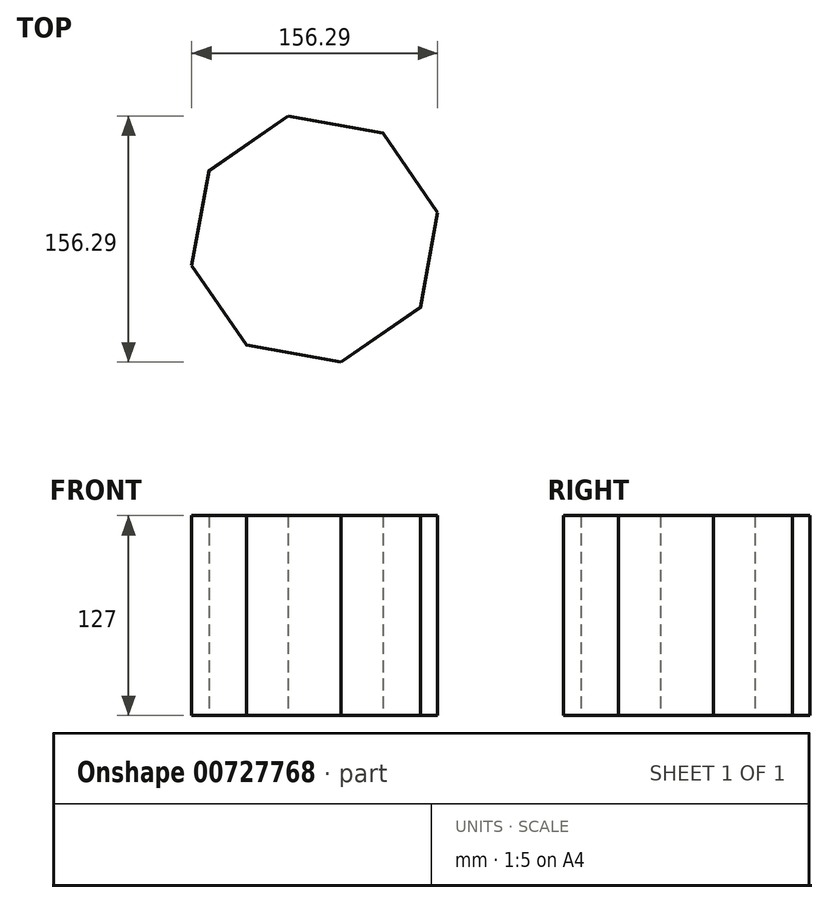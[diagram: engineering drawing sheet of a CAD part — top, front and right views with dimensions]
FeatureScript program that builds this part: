
annotation { "Feature Type Name" : "Feature", "Feature Type Description" : "" }
export const myFeature = defineFeature(function(context is Context, id is Id, definition is map)
    precondition{}
    {
        {
            var Q0;
            Q0=qCreatedBy(makeId("Top.planeOp"),FACE);
            var sketch = newSketch(context, id + "F0", { "sketchPlane" : qUnion([Q0])});
            skCircle(sketch, "E0.cCircle", {"center": v(-104, 22.78) * mm, "radius": 73.86 * mm, "construction": true});
            skLineSegment(sketch, "E0.0", {"start": v(-60.66, 89.95) * mm, "end": v(-25.86, 39.63) * mm});
            skLineSegment(sketch, "E0.1", {"start": v(-25.86, 39.63) * mm, "end": v(-36.84, -20.56) * mm});
            skLineSegment(sketch, "E0.2", {"start": v(-36.84, -20.56) * mm, "end": v(-87.16, -55.36) * mm});
            skLineSegment(sketch, "E0.3", {"start": v(-87.16, -55.36) * mm, "end": v(-147.35, -44.39) * mm});
            skLineSegment(sketch, "E0.4", {"start": v(-147.35, -44.39) * mm, "end": v(-182.15, 5.93) * mm});
            skLineSegment(sketch, "E0.5", {"start": v(-182.15, 5.93) * mm, "end": v(-171.18, 66.13) * mm});
            skLineSegment(sketch, "E0.6", {"start": v(-171.18, 66.13) * mm, "end": v(-120.86, 100.93) * mm});
            skLineSegment(sketch, "E0.7", {"start": v(-120.86, 100.93) * mm, "end": v(-60.66, 89.95) * mm});
            skPoint(sketch, "E0.0.midPoint", {"position": v(-43.26, 64.8) * mm});
            skSolve(sketch);
        }
        {
            var Q0;
            Q0=makeQuery(id+"F0.imprint","IMPRINT",FACE,{"disambiguationData":[TD([[makeQuery(id+"F0.imprint","IMPRINT",EDGE,{"derivedFrom":sQuery(id+"F0.wireOp",EDGE,"E0.0")}),-1.0]])]});
            extrude(context, id + "F1", {"entities" : qUnion([Q0]), "depth" : 127 * mm, "offsetDistance" : 25.4 * mm});
        }
        {
            var Q0;
            Q0=makeQuery(id+"F1.opExtrude","CAP_FACE",FACE,{"disambiguationData":[OSD([sQuery(id+"F0.wireOp",EDGE,"E0.0"),sQuery(id+"F0.wireOp",EDGE,"E0.1"),sQuery(id+"F0.wireOp",EDGE,"E0.2"),sQuery(id+"F0.wireOp",EDGE,"E0.3"),sQuery(id+"F0.wireOp",EDGE,"E0.4"),sQuery(id+"F0.wireOp",EDGE,"E0.5"),sQuery(id+"F0.wireOp",EDGE,"E0.6"),sQuery(id+"F0.wireOp",EDGE,"E0.7")])],"isStart":false});
            shell(context, id + "F2", {"entities" : qUnion([Q0]), "thickness" : 3 / 203.2 * mm});
        }
    });
